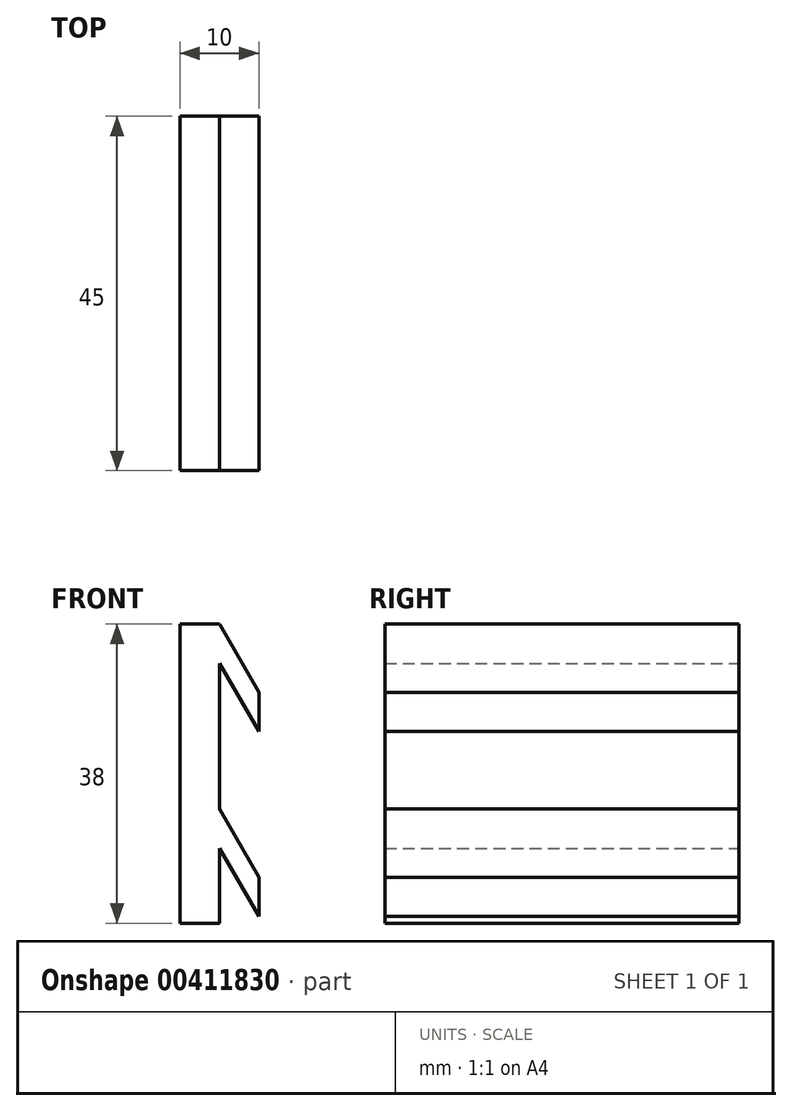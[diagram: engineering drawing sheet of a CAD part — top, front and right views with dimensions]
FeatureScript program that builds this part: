
annotation { "Feature Type Name" : "Feature", "Feature Type Description" : "" }
export const myFeature = defineFeature(function(context is Context, id is Id, definition is map)
    precondition{}
    {
        {
            var Q0;
            Q0=qCreatedBy(makeId("Top.planeOp"),FACE);
            var sketch = newSketch(context, id + "F0", { "sketchPlane" : qUnion([Q0])});
            skLineSegment(sketch, "E0.bottom", {"start": v(2.5, 22.5) * mm, "end": v(-2.5, 22.5) * mm});
            skLineSegment(sketch, "E0.top", {"start": v(2.5, -22.5) * mm, "end": v(-2.5, -22.5) * mm});
            skLineSegment(sketch, "E0.left", {"start": v(2.5, 22.5) * mm, "end": v(2.5, -22.5) * mm});
            skLineSegment(sketch, "E0.right", {"start": v(-2.5, 22.5) * mm, "end": v(-2.5, -22.5) * mm});
            skPoint(sketch, "E0.middle", {"position": v(0, 0) * mm});
            skSolve(sketch);
        }
        {
            var Q0;
            Q0=makeQuery(id+"F0.imprint","IMPRINT",FACE,{"disambiguationData":[TD([[makeQuery(id+"F0.imprint","IMPRINT",EDGE,{"derivedFrom":sQuery(id+"F0.wireOp",EDGE,"E0.bottom")}),1.0]])]});
            extrude(context, id + "F1", {"entities" : qUnion([Q0]), "depth" : 38 * mm});
        }
        {
            var Q0;
            Q0=qCreatedBy(makeId("Front.planeOp"),FACE);
            var sketch = newSketch(context, id + "F2", { "sketchPlane" : qUnion([Q0])});
            skPoint(sketch, "E1.0", {"position": v(2.5, 19) * mm});
            skLineSegment(sketch, "E2.0", {"start": v(2.5, 38) * mm, "end": v(2.5, 0) * mm});
            skLineSegment(sketch, "E3", {"start": v(2.5, 38) * mm, "end": v(7.5, 29.34) * mm});
            skLineSegment(sketch, "E4", {"start": v(7.5, 29.34) * mm, "end": v(7.5, 24.34) * mm});
            skLineSegment(sketch, "E5", {"start": v(7.5, 24.34) * mm, "end": v(2.5, 33) * mm});
            skLineSegment(sketch, "E6.0.1.0", {"start": v(7.5, 5.84) * mm, "end": v(7.5, 0.84) * mm});
            skLineSegment(sketch, "E6.0.1.1", {"start": v(2.5, 14.5) * mm, "end": v(7.5, 5.84) * mm});
            skLineSegment(sketch, "E6.0.1.2", {"start": v(7.5, 0.84) * mm, "end": v(2.5, 9.5) * mm});
            skLineSegment(sketch, "E6.direction1", {"start": v(7.5, 24.34) * mm, "end": v(32.5, 24.34) * mm, "construction": true});
            skLineSegment(sketch, "E6.direction2", {"start": v(7.5, 24.34) * mm, "end": v(7.5, 0.84) * mm, "construction": true});
            skSolve(sketch);
        }
        {
            var Q0;
            {var subQ0=sQuery(id+"F2.wireOp",EDGE,"E3");Q0=makeQuery(id+"F2.imprint","IMPRINT",FACE,{"disambiguationData":[TD([[makeQuery(id+"F2.imprint","IMPRINT",EDGE,{"derivedFrom":subQ0}),-1.0]])]});}
            var Q1;
            Q1=makeQuery(id+"F2.imprint","IMPRINT",FACE,{"disambiguationData":[TD([[makeQuery(id+"F2.imprint","IMPRINT",EDGE,{"derivedFrom":sQuery(id+"F2.wireOp",EDGE,"E6.0.1.0")}),-1.0]])]});
            extrude(context, id + "F3", {"entities" : qUnion([Q0, Q1]), "operationType" : NewBodyOperationType.ADD, "endBound" : BoundingType.SYMMETRIC, "depth" : 45 * mm});
        }
    });
